AUTODESK INVENTOR PART (.ipt)
format: ipt  version: 2020 (Build 240168000, 168)  size: 233,472 bytes
history: native  units: mm
features: sketch x4, extrude x3, projected_geometry x3, pattern_circular x1
ambient origin geometry x8: Origin, YZ Plane, XZ Plane, XY Plane, X Axis, Y Axis, Z Axis, Center Point
bodies: Solid1 (feature_tree)
feature tree (11):
  extrude  "Extrusion1"  Depth=100.0mm
  extrude  "Extrusion2"  Depth=0.3mm
  extrude  "Extrusion3"  Depth=0.3mm TaperAngle=0.0deg
  pattern_circular  "Circular Pattern1"  [2 undecoded]
  sketch  "Sketch4"  dims[d8=7.0mm d9=2.5mm d10=0.2mm d11=8.0mm d12=2.5mm d13=0.2mm d14=12.0mm d15=2.5mm d16=0.2mm d17=0.3mm d18=0.0mm d19=60.0mm d20=360.0deg d22=0.1mm d23=5.0mm d24=4.0mm d25=10.0mm d26=1.2mm d27=3.5mm d28=1.2mm d29=12.0mm d30=13.5mm d31=4.0mm d32=27.0mm]
  sketch  "Sketch1"  dims[d0=100.0mm d1=100.0mm]
  sketch  "Sketch2"  dims[d2=0.3mm d3=0.0mm d4=50.0mm]
  projected_geometry  "Projected Loop1"
  sketch  "Sketch3"  dims[d5=3.0mm d6=0.3mm d7=0.0mm]
  projected_geometry  "Projected Loop2"
  projected_geometry  "Projected Loop3"
note: 2 required parameter values undecoded (feature->parameter linkage not recoverable at this tier; creation-order binding heuristic only, values carry confidence <= 0.55)
